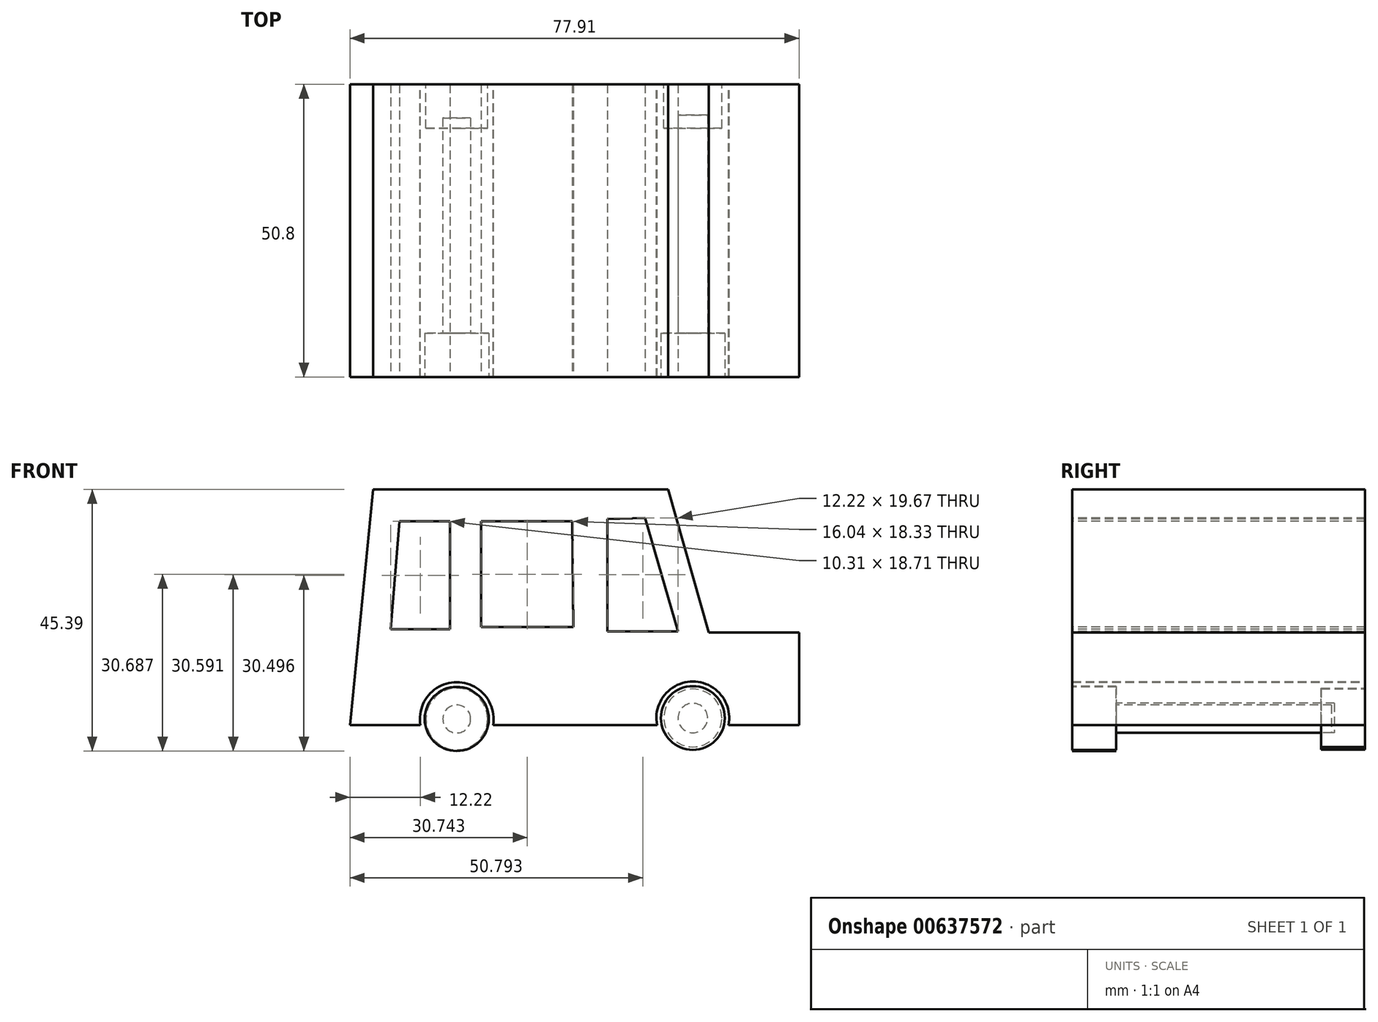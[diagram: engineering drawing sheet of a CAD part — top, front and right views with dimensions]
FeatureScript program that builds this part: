
annotation { "Feature Type Name" : "Feature", "Feature Type Description" : "" }
export const myFeature = defineFeature(function(context is Context, id is Id, definition is map)
    precondition{}
    {
        {
            var Q0;
            Q0=qCreatedBy(makeId("Front.planeOp"),FACE);
            var sketch = newSketch(context, id + "F0", { "sketchPlane" : qUnion([Q0])});
            skLineSegment(sketch, "E0", {"start": v(-41.15, 14.23) * mm, "end": v(36.76, 14.23) * mm});
            skLineSegment(sketch, "E1", {"start": v(36.76, 14.23) * mm, "end": v(36.76, 30.27) * mm});
            skLineSegment(sketch, "E2", {"start": v(36.76, 30.27) * mm, "end": v(21.1, 30.27) * mm});
            skLineSegment(sketch, "E3", {"start": v(21.1, 30.27) * mm, "end": v(14.04, 55.1) * mm});
            skLineSegment(sketch, "E4", {"start": v(14.04, 55.1) * mm, "end": v(-34.09, 55.1) * mm});
            skLineSegment(sketch, "E5", {"start": v(-34.09, 55.1) * mm, "end": v(-37.14, 55.1) * mm});
            skLineSegment(sketch, "E6", {"start": v(-37.14, 55.1) * mm, "end": v(-41.15, 14.23) * mm});
            skArc(sketch, "E7", {"start": v(-16.33, 14.23) * mm, "mid": v(-22.63, 21.65) * mm, "end": v(-28.93, 14.23) * mm});
            skArc(sketch, "E8", {"start": v(24.54, 14.23) * mm, "mid": v(18.33, 21.75) * mm, "end": v(12.13, 14.23) * mm});
            skSolve(sketch);
        }
        {
            var Q0;
            Q0=makeQuery(id+"F0.imprint","IMPRINT",FACE,{"disambiguationData":[TD([[makeQuery(id+"F0.imprint","IMPRINT",EDGE,{"derivedFrom":sQuery(id+"F0.wireOp",EDGE,"E0")}),1.0]])]});
            extrude(context, id + "F1", {"entities" : qUnion([Q0]), "depth" : 50.8 * mm, "offsetDistance" : 25.4 * mm});
        }
        {
            var Q0;
            Q0=makeQuery(id+"F1.opExtrude","CAP_FACE",FACE,{"disambiguationData":[OSD([sQuery(id+"F0.wireOp",EDGE,"E0"),sQuery(id+"F0.wireOp",EDGE,"E1"),sQuery(id+"F0.wireOp",EDGE,"E2"),sQuery(id+"F0.wireOp",EDGE,"E3"),sQuery(id+"F0.wireOp",EDGE,"E4"),sQuery(id+"F0.wireOp",EDGE,"E5"),sQuery(id+"F0.wireOp",EDGE,"E6"),sQuery(id+"F0.wireOp",EDGE,"E7"),sQuery(id+"F0.wireOp",EDGE,"E8")])],"isStart":false});
            var sketch = newSketch(context, id + "F2", { "sketchPlane" : qUnion([Q0])});
            skLineSegment(sketch, "E9", {"start": v(10.03, 50.13) * mm, "end": v(15.75, 30.46) * mm});
            skLineSegment(sketch, "E10", {"start": v(15.75, 30.46) * mm, "end": v(3.53, 30.46) * mm});
            skLineSegment(sketch, "E11", {"start": v(3.53, 30.46) * mm, "end": v(3.53, 49.93) * mm});
            skLineSegment(sketch, "E12", {"start": v(3.53, 49.93) * mm, "end": v(10.03, 50.13) * mm});
            skSolve(sketch);
        }
        {
            var Q0;
            Q0=makeQuery(id+"F2.imprint","IMPRINT",FACE,{"disambiguationData":[TD([[makeQuery(id+"F2.imprint","IMPRINT",EDGE,{"derivedFrom":sQuery(id+"F2.wireOp",EDGE,"E9")}),-1.0]])]});
            extrude(context, id + "F3", {"entities" : qUnion([Q0]), "operationType" : NewBodyOperationType.REMOVE, "oppositeDirection" : true, "depth" : 50.8 * mm, "offsetDistance" : 25.4 * mm});
        }
        {
            var Q0;
            Q0=makeQuery(id+"F1.opExtrude","CAP_FACE",FACE,{"disambiguationData":[OSD([sQuery(id+"F0.wireOp",EDGE,"E0"),sQuery(id+"F0.wireOp",EDGE,"E1"),sQuery(id+"F0.wireOp",EDGE,"E2"),sQuery(id+"F0.wireOp",EDGE,"E3"),sQuery(id+"F0.wireOp",EDGE,"E4"),sQuery(id+"F0.wireOp",EDGE,"E5"),sQuery(id+"F0.wireOp",EDGE,"E6"),sQuery(id+"F0.wireOp",EDGE,"E7"),sQuery(id+"F0.wireOp",EDGE,"E8")])],"isStart":false});
            var sketch = newSketch(context, id + "F4", { "sketchPlane" : qUnion([Q0])});
            skLineSegment(sketch, "E13", {"start": v(-2.39, 31.22) * mm, "end": v(-18.43, 31.22) * mm});
            skLineSegment(sketch, "E14", {"start": v(-18.43, 31.22) * mm, "end": v(-18.43, 49.55) * mm});
            skLineSegment(sketch, "E15", {"start": v(-18.43, 49.55) * mm, "end": v(-2.58, 49.55) * mm});
            skLineSegment(sketch, "E16", {"start": v(-2.58, 49.55) * mm, "end": v(-2.39, 31.22) * mm});
            skSolve(sketch);
        }
        {
            var Q0;
            Q0=makeQuery(id+"F4.imprint","IMPRINT",FACE,{"disambiguationData":[TD([[makeQuery(id+"F4.imprint","IMPRINT",EDGE,{"derivedFrom":sQuery(id+"F4.wireOp",EDGE,"E13")}),-1.0]])]});
            extrude(context, id + "F5", {"entities" : qUnion([Q0]), "operationType" : NewBodyOperationType.REMOVE, "oppositeDirection" : true, "depth" : 50.8 * mm, "offsetDistance" : 25.4 * mm});
        }
        {
            var Q0;
            Q0=makeQuery(id+"F1.opExtrude","CAP_FACE",FACE,{"disambiguationData":[OSD([sQuery(id+"F0.wireOp",EDGE,"E0"),sQuery(id+"F0.wireOp",EDGE,"E1"),sQuery(id+"F0.wireOp",EDGE,"E2"),sQuery(id+"F0.wireOp",EDGE,"E3"),sQuery(id+"F0.wireOp",EDGE,"E4"),sQuery(id+"F0.wireOp",EDGE,"E5"),sQuery(id+"F0.wireOp",EDGE,"E6"),sQuery(id+"F0.wireOp",EDGE,"E7"),sQuery(id+"F0.wireOp",EDGE,"E8")])],"isStart":false});
            var sketch = newSketch(context, id + "F6", { "sketchPlane" : qUnion([Q0])});
            skLineSegment(sketch, "E17", {"start": v(-23.77, 49.55) * mm, "end": v(-23.77, 30.84) * mm});
            skLineSegment(sketch, "E18", {"start": v(-23.77, 30.84) * mm, "end": v(-34.09, 30.84) * mm});
            skLineSegment(sketch, "E19", {"start": v(-34.09, 30.84) * mm, "end": v(-32.56, 49.55) * mm});
            skLineSegment(sketch, "E20", {"start": v(-32.56, 49.55) * mm, "end": v(-23.77, 49.55) * mm});
            skSolve(sketch);
        }
        {
            var Q0;
            Q0 = qSketchRegion(id + "F6", true);
            extrude(context, id + "F7", {"entities" : qUnion([Q0]), "operationType" : NewBodyOperationType.REMOVE, "oppositeDirection" : true, "depth" : 50.8 * mm, "offsetDistance" : 25.4 * mm});
        }
        {
            var Q0;
            Q0=makeQuery(id+"F1.opExtrude","CAP_FACE",FACE,{"disambiguationData":[OSD([sQuery(id+"F0.wireOp",EDGE,"E0"),sQuery(id+"F0.wireOp",EDGE,"E1"),sQuery(id+"F0.wireOp",EDGE,"E2"),sQuery(id+"F0.wireOp",EDGE,"E3"),sQuery(id+"F0.wireOp",EDGE,"E4"),sQuery(id+"F0.wireOp",EDGE,"E5"),sQuery(id+"F0.wireOp",EDGE,"E6"),sQuery(id+"F0.wireOp",EDGE,"E7"),sQuery(id+"F0.wireOp",EDGE,"E8")])],"isStart":false});
            var sketch = newSketch(context, id + "F8", { "sketchPlane" : qUnion([Q0])});
            skCircle(sketch, "E21", {"center": v(-22.63, 15.27) * mm, "radius": 5.57 * mm});
            skSolve(sketch);
        }
        {
            var Q0;
            Q0 = qSketchRegion(id + "F8", true);
            extrude(context, id + "F9", {"entities" : qUnion([Q0]), "oppositeDirection" : true, "depth" : 7.62 * mm, "offsetDistance" : 25.4 * mm});
        }
        {
            var Q0;
            Q0=makeQuery(id+"F1.opExtrude","CAP_FACE",FACE,{"disambiguationData":[OSD([sQuery(id+"F0.wireOp",EDGE,"E0"),sQuery(id+"F0.wireOp",EDGE,"E1"),sQuery(id+"F0.wireOp",EDGE,"E2"),sQuery(id+"F0.wireOp",EDGE,"E3"),sQuery(id+"F0.wireOp",EDGE,"E4"),sQuery(id+"F0.wireOp",EDGE,"E5"),sQuery(id+"F0.wireOp",EDGE,"E6"),sQuery(id+"F0.wireOp",EDGE,"E7"),sQuery(id+"F0.wireOp",EDGE,"E8")])],"isStart":true});
            var sketch = newSketch(context, id + "F10", { "sketchPlane" : qUnion([Q0])});
            skCircle(sketch, "E22", {"center": v(-18.33, 15.43) * mm, "radius": 5.03 * mm});
            skSolve(sketch);
        }
        {
            var Q0;
            Q0 = qSketchRegion(id + "F10", true);
            extrude(context, id + "F11", {"entities" : qUnion([Q0]), "oppositeDirection" : true, "depth" : 7.62 * mm, "offsetDistance" : 25.4 * mm});
        }
        {
            var Q0;
            Q0=makeQuery(id+"F1.opExtrude","CAP_FACE",FACE,{"disambiguationData":[OSD([sQuery(id+"F0.wireOp",EDGE,"E0"),sQuery(id+"F0.wireOp",EDGE,"E1"),sQuery(id+"F0.wireOp",EDGE,"E2"),sQuery(id+"F0.wireOp",EDGE,"E3"),sQuery(id+"F0.wireOp",EDGE,"E4"),sQuery(id+"F0.wireOp",EDGE,"E5"),sQuery(id+"F0.wireOp",EDGE,"E6"),sQuery(id+"F0.wireOp",EDGE,"E7"),sQuery(id+"F0.wireOp",EDGE,"E8")])],"isStart":false});
            var sketch = newSketch(context, id + "F12", { "sketchPlane" : qUnion([Q0])});
            skCircle(sketch, "E23", {"center": v(18.33, 15.43) * mm, "radius": 5.53 * mm});
            skSolve(sketch);
        }
        {
            var Q0;
            Q0 = qSketchRegion(id + "F12", true);
            extrude(context, id + "F13", {"entities" : qUnion([Q0]), "oppositeDirection" : true, "depth" : 7.62 * mm, "offsetDistance" : 25.4 * mm});
        }
        {
            var Q0;
            Q0=makeQuery(id+"F1.opExtrude","CAP_FACE",FACE,{"disambiguationData":[OSD([sQuery(id+"F0.wireOp",EDGE,"E0"),sQuery(id+"F0.wireOp",EDGE,"E1"),sQuery(id+"F0.wireOp",EDGE,"E2"),sQuery(id+"F0.wireOp",EDGE,"E3"),sQuery(id+"F0.wireOp",EDGE,"E4"),sQuery(id+"F0.wireOp",EDGE,"E5"),sQuery(id+"F0.wireOp",EDGE,"E6"),sQuery(id+"F0.wireOp",EDGE,"E7"),sQuery(id+"F0.wireOp",EDGE,"E8")])],"isStart":true});
            var sketch = newSketch(context, id + "F14", { "sketchPlane" : qUnion([Q0])});
            skCircle(sketch, "E24", {"center": v(22.63, 15.27) * mm, "radius": 5.34 * mm});
            skSolve(sketch);
        }
        {
            var Q0;
            Q0 = qSketchRegion(id + "F14", true);
            extrude(context, id + "F15", {"entities" : qUnion([Q0]), "oppositeDirection" : true, "depth" : 7.62 * mm, "offsetDistance" : 25.4 * mm});
        }
        {
            var Q0;
            Q0=makeQuery(id+"F9.opExtrude","CAP_FACE",FACE,{"disambiguationData":[OSD([sQuery(id+"F8.wireOp",EDGE,"E21")])],"isStart":false});
            var sketch = newSketch(context, id + "F16", { "sketchPlane" : qUnion([Q0])});
            skCircle(sketch, "E25", {"center": v(22.63, 15.27) * mm, "radius": 2.42 * mm});
            skSolve(sketch);
        }
        {
            var Q0;
            Q0 = qSketchRegion(id + "F16", true);
            extrude(context, id + "F17", {"entities" : qUnion([Q0]), "depth" : 37.34 * mm, "offsetDistance" : 25.4 * mm});
        }
        {
            var Q0;
            Q0=makeQuery(id+"F13.opExtrude","CAP_FACE",FACE,{"disambiguationData":[OSD([sQuery(id+"F12.wireOp",EDGE,"E23")])],"isStart":false});
            var sketch = newSketch(context, id + "F18", { "sketchPlane" : qUnion([Q0])});
            skCircle(sketch, "E26", {"center": v(-18.33, 15.43) * mm, "radius": 2.56 * mm});
            skSolve(sketch);
        }
        {
            var Q0;
            Q0 = qSketchRegion(id + "F18", true);
            extrude(context, id + "F19", {"entities" : qUnion([Q0]), "depth" : 37.85 * mm, "offsetDistance" : 25.4 * mm});
        }
    });
